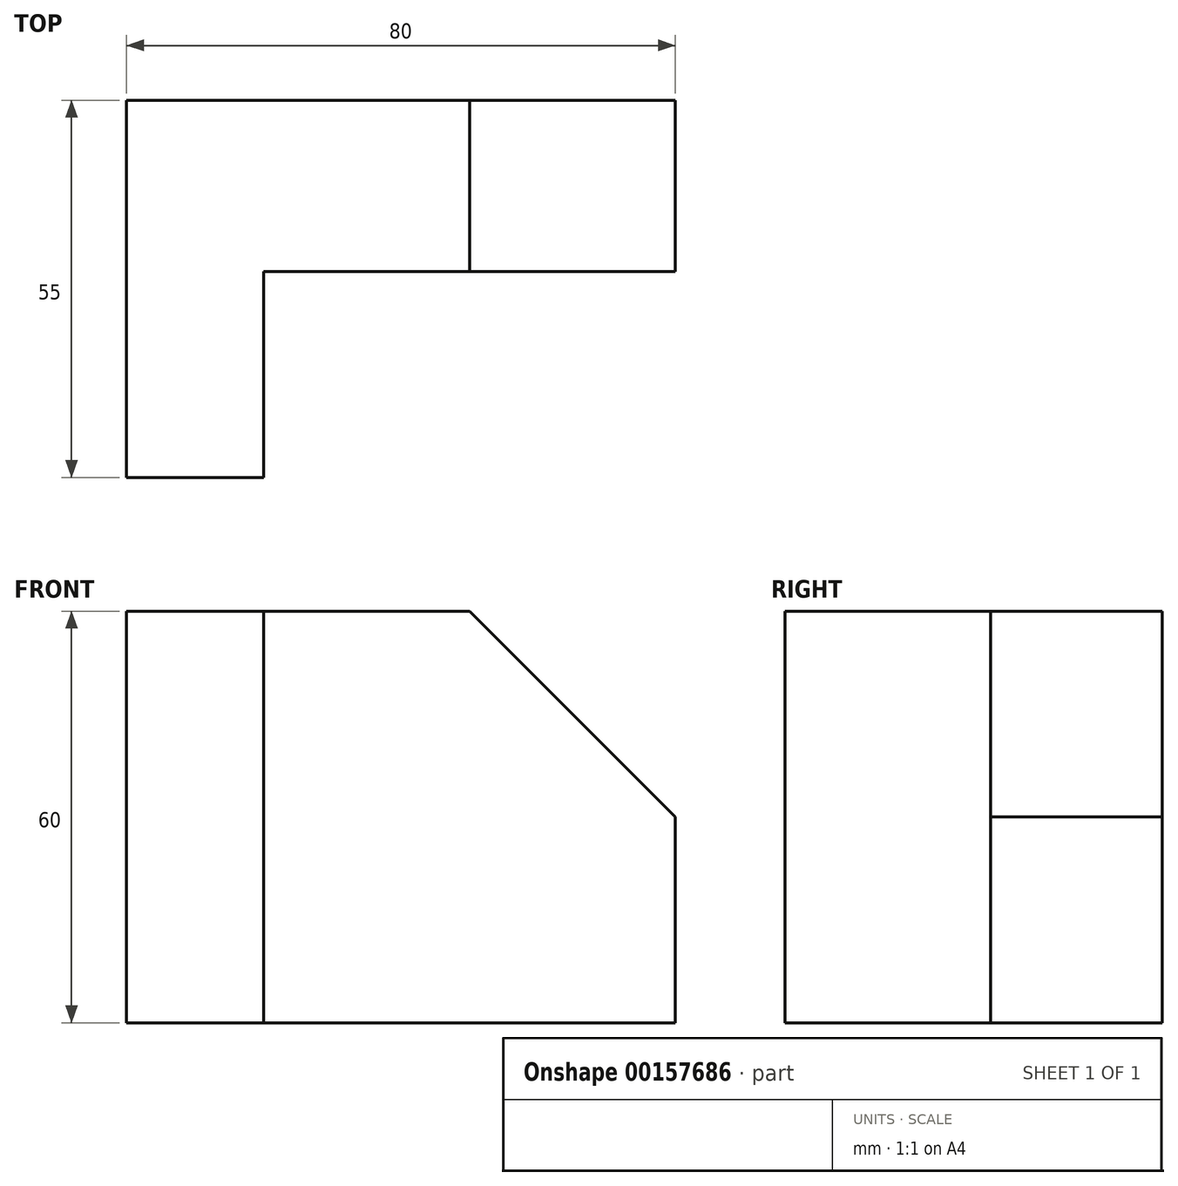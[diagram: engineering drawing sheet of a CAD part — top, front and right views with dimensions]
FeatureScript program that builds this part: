
annotation { "Feature Type Name" : "Feature", "Feature Type Description" : "" }
export const myFeature = defineFeature(function(context is Context, id is Id, definition is map)
    precondition{}
    {
        {
            var Q0;
            Q0=qCreatedBy(makeId("Front.planeOp"),FACE);
            var sketch = newSketch(context, id + "F0", { "sketchPlane" : qUnion([Q0])});
            skLineSegment(sketch, "E0.top", {"start": v(-40, -30) * mm, "end": v(40, -30) * mm});
            skLineSegment(sketch, "E0.left", {"start": v(-40, 30) * mm, "end": v(-40, -30) * mm});
            skPoint(sketch, "E0.middle", {"position": v(0, 0) * mm});
            skPoint(sketch, "E0.right.start.orphan", {"position": v(40, 30) * mm});
            skLineSegment(sketch, "E1", {"start": v(40, -30) * mm, "end": v(40, 0) * mm});
            skLineSegment(sketch, "E2", {"start": v(-40, 30) * mm, "end": v(10, 30) * mm});
            skLineSegment(sketch, "E3", {"start": v(10, 30) * mm, "end": v(40, 0) * mm});
            skSolve(sketch);
        }
        {
            var Q0;
            Q0 = qSketchRegion(id + "F0", true);
            extrude(context, id + "F1", {"entities" : qUnion([Q0]), "depth" : 25 * mm});
        }
        {
            var Q0;
            Q0=makeQuery(id+"F1.opExtrude","CAP_FACE",FACE,{"disambiguationData":[OSD([sQuery(id+"F0.wireOp",EDGE,"E0.top"),sQuery(id+"F0.wireOp",EDGE,"E0.left"),sQuery(id+"F0.wireOp",EDGE,"E1"),sQuery(id+"F0.wireOp",EDGE,"E2"),sQuery(id+"F0.wireOp",EDGE,"E3")])],"isStart":false});
            var sketch = newSketch(context, id + "F2", { "sketchPlane" : qUnion([Q0])});
            skLineSegment(sketch, "E4", {"start": v(-20, 30) * mm, "end": v(-20, -30) * mm});
            skLineSegment(sketch, "E5", {"start": v(-40, -30) * mm, "end": v(-20, -30) * mm});
            skSolve(sketch);
        }
        {
            var Q0;
            Q0 = qSketchRegion(id + "F2", true);
            var Q1;
            {var subQ0=sQuery(id+"F2.wireOp",EDGE,"E4");Q1=makeQuery(id+"F2.imprint","IMPRINT",FACE,{"disambiguationData":[TD([[makeQuery(id+"F2.imprint","IMPRINT",EDGE,{"derivedFrom":subQ0}),-1.0]])]});}
            extrude(context, id + "F3", {"entities" : qUnion([Q0, Q1]), "operationType" : NewBodyOperationType.ADD, "depth" : 30 * mm});
        }
    });
